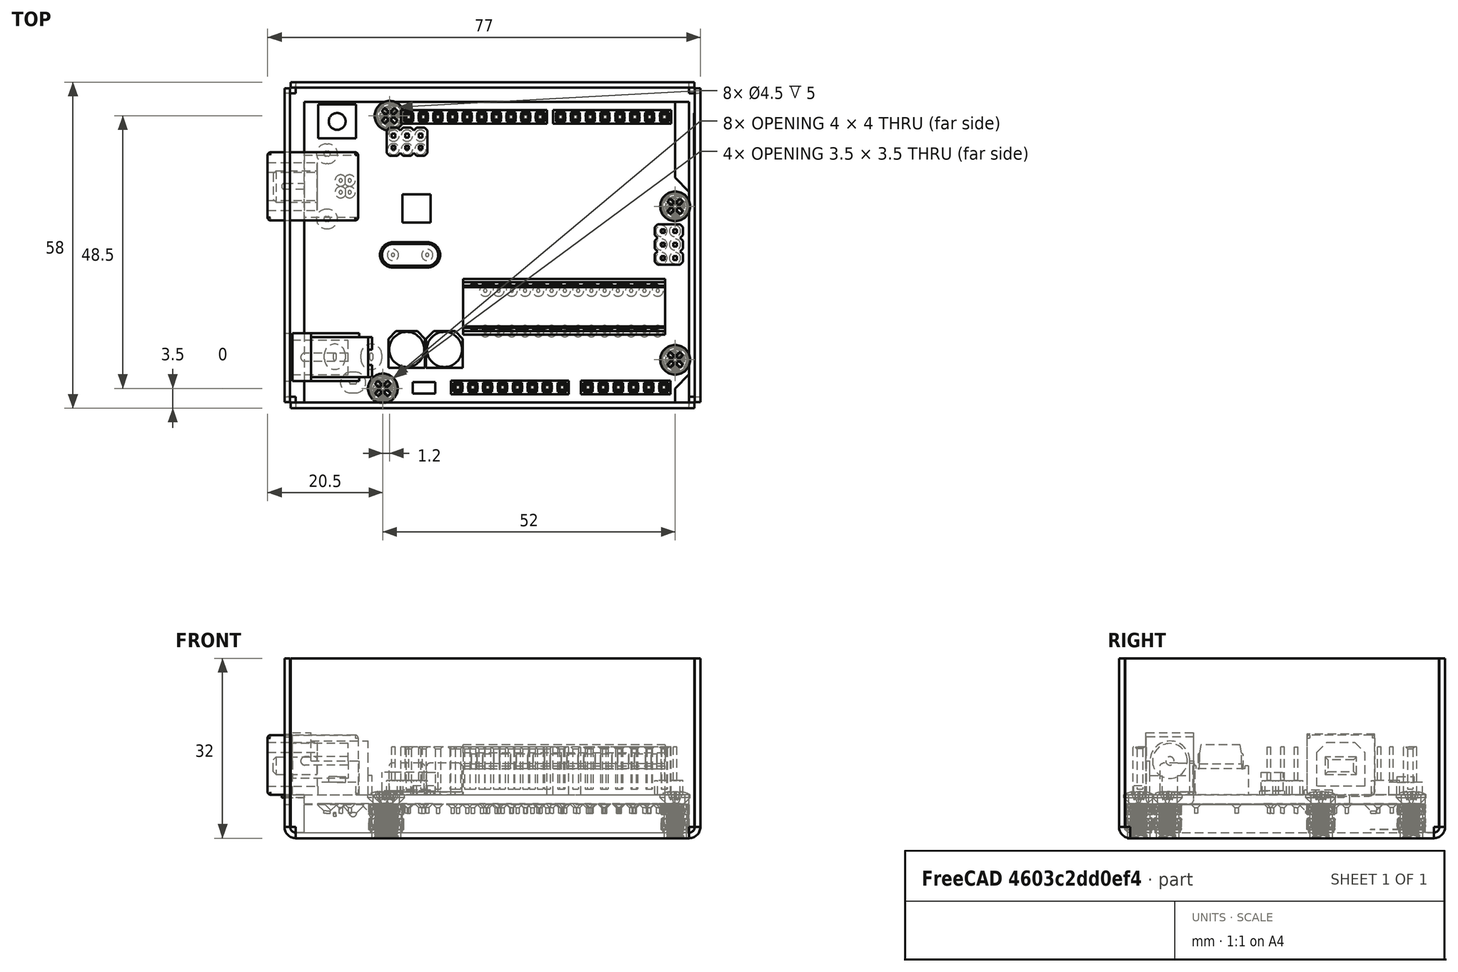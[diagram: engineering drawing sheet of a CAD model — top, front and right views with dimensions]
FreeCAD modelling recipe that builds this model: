
FCSTD DOCUMENT  (FreeCAD 0.20R29603 (Git))
Label: Arduino Enclosure Assembly V2
License: All rights reserved
LicenseURL: http://en.wikipedia.org/wiki/All_rights_reserved
objects: App::FeaturePython×15, Part::FeaturePython×12, PartDesign::ShapeBinder×1, Sketcher::SketchObject×1, PartDesign::Body×1
note: 15 computed .brp shape members not serialized (recipe doc carries the construction recipe); baked Part::Feature solids carry a one-line shape summary decoded from their .brp

FEATURE [Part::FeaturePython] b_Arduino_Sheet_Metal_Enclosure_001_  label="Arduino Sheet Metal Enclosure_001"  # a2plus imported part (geometry in sourceFile) (typed FeaturePython)
  a2p_Version = 0.4.60n
  fixedPosition = true
  objectType = a2pPart
  sourceFile = .\Arduino Sheet Metal Enclosure.FCStd
  subassemblyImport = false
  timeLastImport = 1.68621e+09
  updateColors = true
FEATURE [Part::FeaturePython] b_M3_Heat_Insert_001_  label="M3 Heat Insert_001"  # a2plus imported part (geometry in sourceFile) (typed FeaturePython)
  Placement = pos=(-18.2999,23.4999,3.2814e-09) rot=(0,0,1;0rad)
  a2p_Version = 0.4.60n
  fixedPosition = false
  objectType = a2pPart
  sourceFile = .\M3 Heat Insert.FCStd
  subassemblyImport = false
  timeLastImport = 1.68602e+09
  updateColors = true
FEATURE [App::FeaturePython] centerOfMass_001  label="centerOfMass_001__Arduino Sheet Metal Enclosure_001"  # a2plus constraint (typed FeaturePython)
  Object1 = b_M3_Heat_Insert_001_
  Object2 = b_Arduino_Sheet_Metal_Enclosure_001_
  ParentTreeObject = -> b_M3_Heat_Insert_001_
  SubElement1 = Edge31
  SubElement2 = Edge85
  Suppressed = false
  Type = CenterOfMass
  directionConstraint = 0
  lockRotation = false
  offset = 0
FEATURE [App::FeaturePython] centerOfMass_001_mirror  label="centerOfMass_001__M3 Heat Insert_001"  # a2plus constraint (typed FeaturePython)
  Object1 = b_M3_Heat_Insert_001_
  Object2 = b_Arduino_Sheet_Metal_Enclosure_001_
  ParentTreeObject = -> b_Arduino_Sheet_Metal_Enclosure_001_
  SubElement1 = Edge31
  SubElement2 = Edge85
  Suppressed = false
  Type = CenterOfMass
  directionConstraint = 0
  lockRotation = false
  offset = 0
FEATURE [Part::FeaturePython] b_M3_Heat_Insert_001_001  label="M3 Heat Insert_002"  # a2plus imported part (geometry in sourceFile) (typed FeaturePython)
  Placement = pos=(-19.4999,-25.0001,3.76836e-09) rot=(0,0,1;0rad)
  a2p_Version = 0.4.60n
  fixedPosition = false
  objectType = a2pPart
  sourceFile = .\M3 Heat Insert.FCStd
  subassemblyImport = false
  timeLastImport = 1.68602e+09
  updateColors = true
FEATURE [App::FeaturePython] centerOfMass_002  label="centerOfMass_002__Arduino Sheet Metal Enclosure_001"  # a2plus constraint (typed FeaturePython)
  Object1 = b_M3_Heat_Insert_001_001
  Object2 = b_Arduino_Sheet_Metal_Enclosure_001_
  ParentTreeObject = -> b_M3_Heat_Insert_001_001
  SubElement1 = Edge31
  SubElement2 = Edge86
  Suppressed = false
  Type = CenterOfMass
  directionConstraint = 0
  lockRotation = false
  offset = 0
FEATURE [App::FeaturePython] centerOfMass_002_mirror  label="centerOfMass_002__M3 Heat Insert_002"  # a2plus constraint (typed FeaturePython)
  Object1 = b_M3_Heat_Insert_001_001
  Object2 = b_Arduino_Sheet_Metal_Enclosure_001_
  ParentTreeObject = -> b_Arduino_Sheet_Metal_Enclosure_001_
  SubElement1 = Edge31
  SubElement2 = Edge86
  Suppressed = false
  Type = CenterOfMass
  directionConstraint = 0
  lockRotation = false
  offset = 0
FEATURE [Part::FeaturePython] b_M3_Heat_Insert_001_002  label="M3 Heat Insert_003"  # a2plus imported part (geometry in sourceFile) (typed FeaturePython)
  Placement = pos=(32.5001,7.39989,1.94646e-09) rot=(0,0,1;0rad)
  a2p_Version = 0.4.60n
  fixedPosition = false
  objectType = a2pPart
  sourceFile = .\M3 Heat Insert.FCStd
  subassemblyImport = false
  timeLastImport = 1.68602e+09
  updateColors = true
FEATURE [App::FeaturePython] centerOfMass_003  label="centerOfMass_003__Arduino Sheet Metal Enclosure_001"  # a2plus constraint (typed FeaturePython)
  Object1 = b_M3_Heat_Insert_001_002
  Object2 = b_Arduino_Sheet_Metal_Enclosure_001_
  ParentTreeObject = -> b_M3_Heat_Insert_001_002
  SubElement1 = Edge31
  SubElement2 = Edge84
  Suppressed = false
  Type = CenterOfMass
  directionConstraint = 0
  lockRotation = false
  offset = 0
FEATURE [App::FeaturePython] centerOfMass_003_mirror  label="centerOfMass_003__M3 Heat Insert_003"  # a2plus constraint (typed FeaturePython)
  Object1 = b_M3_Heat_Insert_001_002
  Object2 = b_Arduino_Sheet_Metal_Enclosure_001_
  ParentTreeObject = -> b_Arduino_Sheet_Metal_Enclosure_001_
  SubElement1 = Edge31
  SubElement2 = Edge84
  Suppressed = false
  Type = CenterOfMass
  directionConstraint = 0
  lockRotation = false
  offset = 0
FEATURE [Part::FeaturePython] b_M3_Heat_Insert_001_003  label="M3 Heat Insert_004"  # a2plus imported part (geometry in sourceFile) (typed FeaturePython)
  Placement = pos=(32.5001,-19.9001,1.94621e-09) rot=(0,0,1;0rad)
  a2p_Version = 0.4.60n
  fixedPosition = false
  objectType = a2pPart
  sourceFile = .\M3 Heat Insert.FCStd
  subassemblyImport = false
  timeLastImport = 1.68602e+09
  updateColors = true
FEATURE [App::FeaturePython] centerOfMass_004  label="centerOfMass_004__Arduino Sheet Metal Enclosure_001"  # a2plus constraint (typed FeaturePython)
  Object1 = b_M3_Heat_Insert_001_003
  Object2 = b_Arduino_Sheet_Metal_Enclosure_001_
  ParentTreeObject = -> b_M3_Heat_Insert_001_003
  SubElement1 = Edge31
  SubElement2 = Edge83
  Suppressed = false
  Type = CenterOfMass
  directionConstraint = 0
  lockRotation = false
  offset = 0
FEATURE [App::FeaturePython] centerOfMass_004_mirror  label="centerOfMass_004__M3 Heat Insert_004"  # a2plus constraint (typed FeaturePython)
  Object1 = b_M3_Heat_Insert_001_003
  Object2 = b_Arduino_Sheet_Metal_Enclosure_001_
  ParentTreeObject = -> b_Arduino_Sheet_Metal_Enclosure_001_
  SubElement1 = Edge31
  SubElement2 = Edge83
  Suppressed = false
  Type = CenterOfMass
  directionConstraint = 0
  lockRotation = false
  offset = 0
FEATURE [Part::FeaturePython] b_Uno_STp_001_  label="Uno STp_001"  # a2plus imported part (geometry in sourceFile) (typed FeaturePython)
  Placement = pos=(-0.5,-0.75,6.14415) rot=(0,0,1;1.5708rad)
  a2p_Version = 0.4.60n
  fixedPosition = false
  objectType = a2pPart
  sourceFile = .\Uno STp.FCStd
  subassemblyImport = false
  timeLastImport = 1.68621e+09
  updateColors = true
FEATURE [App::FeaturePython] axisCoincident_001  label="axisCoincident_001__Arduino Sheet Metal Enclosure_001"  # a2plus constraint (typed FeaturePython)
  Object1 = b_Uno_STp_001_
  Object2 = b_Arduino_Sheet_Metal_Enclosure_001_
  ParentTreeObject = -> b_Uno_STp_001_
  SubElement1 = Edge244
  SubElement2 = Edge86
  Suppressed = false
  Type = axial
  directionConstraint = 1
  lockRotation = false
FEATURE [App::FeaturePython] axisCoincident_001_mirror  label="axisCoincident_001__Uno STp_001"  # a2plus constraint (typed FeaturePython)
  Object1 = b_Uno_STp_001_
  Object2 = b_Arduino_Sheet_Metal_Enclosure_001_
  ParentTreeObject = -> b_Arduino_Sheet_Metal_Enclosure_001_
  SubElement1 = Edge244
  SubElement2 = Edge86
  Suppressed = false
  Type = axial
  directionConstraint = 1
  lockRotation = false
FEATURE [Part::FeaturePython] Screw  label="M3x5-Screw"  # Fasteners workbench fastener (typed FeaturePython)
  Placement = pos=(32.5,7.4,7.74415) rot=(0,0,1;0rad)
  baseObject = -> b_Uno_STp_001_ [Edge239]
  diameter = 4
  invert = true
  leftHanded = false
  length = 1
  lengthCustom = 5
  matchOuter = false
  offset = 0
  thread = false
  type = 48
FEATURE [Part::FeaturePython] Screw001  label="M3x5-Screw007"  # Fasteners workbench fastener (typed FeaturePython)
  Placement = pos=(32.5,-19.9,7.74415) rot=(0,0,1;0rad)
  baseObject = -> b_Uno_STp_001_ [Edge333]
  diameter = 4
  invert = true
  leftHanded = false
  length = 1
  lengthCustom = 5
  matchOuter = false
  offset = 0
  thread = false
  type = 48
FEATURE [Part::FeaturePython] Screw002  label="M3x5-Screw006"  # Fasteners workbench fastener (typed FeaturePython)
  Placement = pos=(-18.3,23.5,7.74415) rot=(0,0,1;0rad)
  baseObject = -> b_Uno_STp_001_ [Edge242]
  diameter = 4
  invert = true
  leftHanded = false
  length = 1
  lengthCustom = 5
  matchOuter = false
  offset = 0
  thread = false
  type = 48
FEATURE [App::FeaturePython] centerOfMass_005_mirror  label="centerOfMass_005__M3x5-Screw003"  # a2plus constraint (typed FeaturePython)
  Object1 = Screw003
  Object2 = b_Arduino_Sheet_Metal_Enclosure_001_001
  SubElement1 = Edge64
  SubElement2 = Edge93
  Suppressed = false
  Type = CenterOfMass
  directionConstraint = 1
  lockRotation = false
  offset = 0
FEATURE [Part::FeaturePython] Screw003  label="M3x6-Screw"  # Fasteners workbench fastener (typed FeaturePython)
  Placement = pos=(-19.5,-25,7.74415) rot=(0,0,1;0rad)
  baseObject = -> b_Uno_STp_001_ [Edge243]
  diameter = 4
  invert = true
  leftHanded = false
  length = 2
  lengthCustom = 6
  matchOuter = false
  offset = 0
  thread = false
  type = 48
FEATURE [Part::FeaturePython] b_Arduino_Sheet_Metal_Enclosure_001_001003  label="Arduino Sheet Metal Enclosure_002"  # a2plus imported part (geometry in sourceFile) (typed FeaturePython)
  Placement = pos=(-1.922e-08,-1.25944e-08,4.4218e-09) rot=(0,0,1;0rad)
  a2p_Version = 0.4.60n
  fixedPosition = false
  objectType = a2pPart
  sourceFile = .\Arduino Sheet Metal Enclosure.FCStd
  subassemblyImport = false
  timeLastImport = 1.68621e+09
  updateColors = true
FEATURE [App::FeaturePython] centerOfMass_006  label="centerOfMass_006__M3 Heat Insert_002"  # a2plus constraint (typed FeaturePython)
  Object1 = b_Arduino_Sheet_Metal_Enclosure_001_001003
  Object2 = b_M3_Heat_Insert_001_001
  ParentTreeObject = -> b_Arduino_Sheet_Metal_Enclosure_001_001003
  SubElement1 = Edge165
  SubElement2 = Edge31
  Suppressed = false
  Type = CenterOfMass
  directionConstraint = 0
  lockRotation = false
  offset = 0
FEATURE [App::FeaturePython] centerOfMass_006_mirror  label="centerOfMass_006__Arduino Sheet Metal Enclosure_002"  # a2plus constraint (typed FeaturePython)
  Object1 = b_Arduino_Sheet_Metal_Enclosure_001_001003
  Object2 = b_M3_Heat_Insert_001_001
  ParentTreeObject = -> b_M3_Heat_Insert_001_001
  SubElement1 = Edge165
  SubElement2 = Edge31
  Suppressed = false
  Type = CenterOfMass
  directionConstraint = 0
  lockRotation = false
  offset = 0
FEATURE [Part::FeaturePython] b_Arduino_Sheet_Metal_Enclosure_001_001004  label="Arduino Sheet Metal Enclosure_003"  # a2plus imported part (geometry in sourceFile) (typed FeaturePython)
  Placement = pos=(4.57066e-07,-4.01067e-06,-5.06575e-07) rot=(0,0,1;0rad)
  a2p_Version = 0.4.60n
  fixedPosition = false
  objectType = a2pPart
  sourceFile = .\Arduino Sheet Metal Enclosure.FCStd
  subassemblyImport = false
  timeLastImport = 1.68621e+09
  updateColors = true
FEATURE [App::FeaturePython] centerOfMass_005  label="centerOfMass_005__Arduino Sheet Metal Enclosure_003"  # a2plus constraint (typed FeaturePython)
  Object1 = b_M3_Heat_Insert_001_001
  Object2 = b_Arduino_Sheet_Metal_Enclosure_001_001004
  ParentTreeObject = -> b_M3_Heat_Insert_001_001
  SubElement1 = Edge31
  SubElement2 = Edge165
  Suppressed = false
  Type = CenterOfMass
  directionConstraint = 0
  lockRotation = false
  offset = 0
FEATURE [App::FeaturePython] centerOfMass_005_mirror001  label="centerOfMass_005__M3 Heat Insert_002"  # a2plus constraint (typed FeaturePython)
  Object1 = b_M3_Heat_Insert_001_001
  Object2 = b_Arduino_Sheet_Metal_Enclosure_001_001004
  ParentTreeObject = -> b_Arduino_Sheet_Metal_Enclosure_001_001004
  SubElement1 = Edge31
  SubElement2 = Edge165
  Suppressed = false
  Type = CenterOfMass
  directionConstraint = 0
  lockRotation = false
  offset = 0
FEATURE [PartDesign::ShapeBinder] Referenceb_Arduino_Sheet_Metal_Enclosure_001_001004
  Placement = pos=(4.57066e-07,-4.01067e-06,-5.06575e-07) rot=(0,0,1;0rad)
  Support = -> [b_Arduino_Sheet_Metal_Enclosure_001_001004]
  TraceSupport = false
FEATURE [Sketcher::SketchObject] Sketch
  FullyConstrained = true
  MapMode = 5
  Placement = pos=(37,-4.01067e-06,-5.06575e-07) rot=(0.57735,0.57735,0.57735;2.0944rad)
  Support = -> [Referenceb_Arduino_Sheet_Metal_Enclosure_001_001004]
FEATURE [PartDesign::Body] Body
  Group = -> [Referenceb_Arduino_Sheet_Metal_Enclosure_001_001004,Sketch]
  Origin = -> Origin
